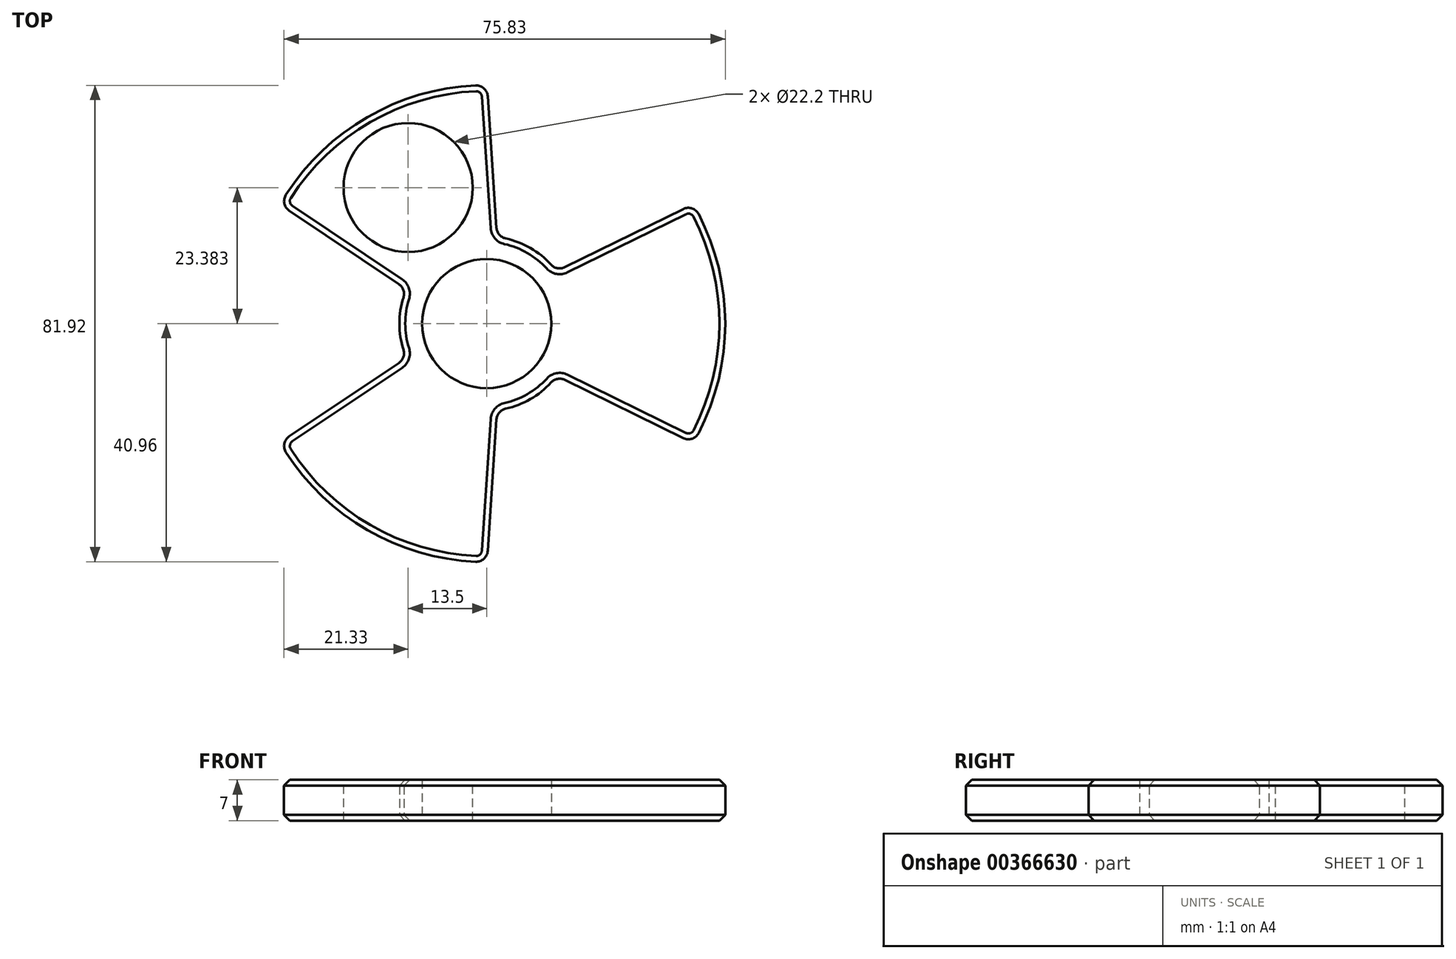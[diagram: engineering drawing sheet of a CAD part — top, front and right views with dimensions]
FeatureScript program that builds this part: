
annotation { "Feature Type Name" : "Feature", "Feature Type Description" : "" }
export const myFeature = defineFeature(function(context is Context, id is Id, definition is map)
    precondition{}
    {
        {
            var Q0;
            Q0=qCreatedBy(makeId("Top.planeOp"),FACE);
            var sketch = newSketch(context, id + "F0", { "sketchPlane" : qUnion([Q0])});
            skCircle(sketch, "E0", {"center": v(0, 0) * mm, "radius": 15 * mm});
            skCircle(sketch, "E1", {"center": v(0, 0) * mm, "radius": 41 * mm});
            skCircle(sketch, "E2", {"center": v(0, 0) * mm, "radius": 11.1 * mm});
            skLineSegment(sketch, "E3", {"start": v(0, 15) * mm, "end": v(0, 41) * mm});
            skLineSegment(sketch, "E4.1.0", {"start": v(-13, 7.5) * mm, "end": v(-35.5, 20.5) * mm});
            skLineSegment(sketch, "E4.2.0", {"start": v(-13, -7.5) * mm, "end": v(-35.5, -20.5) * mm});
            skLineSegment(sketch, "E4.3.0", {"start": v(0, -15) * mm, "end": v(0, -41) * mm});
            skLineSegment(sketch, "E4.4.0", {"start": v(13, -7.5) * mm, "end": v(35.5, -20.5) * mm});
            skLineSegment(sketch, "E4.5.0", {"start": v(13, 7.5) * mm, "end": v(35.5, 20.5) * mm});
            skSolve(sketch);
        }
        {
            var Q0;
            {var subQ0=sQuery(id+"F0.wireOp",EDGE,"E3");Q0=makeQuery(id+"F0.imprint","IMPRINT",FACE,{"disambiguationData":[TD([[makeQuery(id+"F0.imprint","IMPRINT",EDGE,{"derivedFrom":subQ0}),1.0]])]});}
            var Q1;
            {var subQ0=sQuery(id+"F0.wireOp",EDGE,"E4.4.0");Q1=makeQuery(id+"F0.imprint","IMPRINT",FACE,{"disambiguationData":[TD([[makeQuery(id+"F0.imprint","IMPRINT",EDGE,{"derivedFrom":subQ0}),1.0]])]});}
            var Q2;
            {var subQ0=sQuery(id+"F0.wireOp",EDGE,"E4.2.0");Q2=makeQuery(id+"F0.imprint","IMPRINT",FACE,{"disambiguationData":[TD([[makeQuery(id+"F0.imprint","IMPRINT",EDGE,{"derivedFrom":subQ0}),1.0]])]});}
            var Q3;
            Q3=makeQuery(id+"F0.imprint","IMPRINT",FACE,{"disambiguationData":[TD([[makeQuery(id+"F0.imprint","IMPRINT",EDGE,{"derivedFrom":sQuery(id+"F0.wireOp",EDGE,"E2")}),-1.0]])]});
            extrude(context, id + "F1", {"entities" : qUnion([Q0, Q1, Q2, Q3]), "depth" : 7 * mm});
        }
        {
            var Q0;
            Q0=makeQuery(id+"F1.opExtrude","SWEPT_EDGE",EDGE,{"disambiguationData":[OSD([sQuery(id+"F0.wireOp",EDGE,"E0"),sQuery(id+"F0.wireOp",EDGE,"E4.1.0")])]});
            var Q1;
            Q1=makeQuery(id+"F1.opExtrude","SWEPT_EDGE",EDGE,{"disambiguationData":[OSD([sQuery(id+"F0.wireOp",EDGE,"E0"),sQuery(id+"F0.wireOp",EDGE,"E4.2.0")])]});
            var Q2;
            Q2=makeQuery(id+"F1.opExtrude","SWEPT_EDGE",EDGE,{"disambiguationData":[OSD([sQuery(id+"F0.wireOp",EDGE,"E0"),sQuery(id+"F0.wireOp",EDGE,"E4.3.0")])]});
            var Q3;
            Q3=makeQuery(id+"F1.opExtrude","SWEPT_EDGE",EDGE,{"disambiguationData":[OSD([sQuery(id+"F0.wireOp",EDGE,"E0"),sQuery(id+"F0.wireOp",EDGE,"E4.5.0")])]});
            chamfer(context, id + "F2", {"entities" : qUnion([Q0, Q1, Q2, Q3]), "chamferType" : ChamferType.TWO_OFFSETS, "width1" : 5 * mm, "oppositeDirection" : false, "width2" : 27 * mm, "tangentPropagation" : true});
        }
        {
            var Q0;
            Q0=makeQuery(id+"F1.opExtrude","SWEPT_EDGE",EDGE,{"disambiguationData":[OSD([sQuery(id+"F0.wireOp",EDGE,"E0"),sQuery(id+"F0.wireOp",EDGE,"E4.4.0")])]});
            var Q1;
            Q1=makeQuery(id+"F1.opExtrude","SWEPT_EDGE",EDGE,{"disambiguationData":[OSD([sQuery(id+"F0.wireOp",EDGE,"E0"),sQuery(id+"F0.wireOp",EDGE,"E3")])]});
            chamfer(context, id + "F3", {"entities" : qUnion([Q0, Q1]), "chamferType" : ChamferType.TWO_OFFSETS, "width1" : 27 * mm, "oppositeDirection" : false, "width2" : 5 * mm, "tangentPropagation" : true});
        }
        {
            var Q0;
            {var subQ0=sQuery(id+"F0.wireOp",EDGE,"E1");var subQ1=sQuery(id+"F0.wireOp",EDGE,"E4.1.0");Q0=makeQuery(id+"F2.opChamfer","BLEND_EDGE",EDGE,{"blendedFrom":[makeQuery(id+"F1.opExtrude","SWEPT_EDGE",EDGE,{"disambiguationData":[OSD([sQuery(id+"F0.wireOp",EDGE,"E0"),subQ1])]}),makeQuery(id+"F1.opExtrude","SWEPT_FACE",FACE,{"disambiguationData":[OSD([subQ0]),TDD([makeQuery(id+"F0.imprint","IMPRINT",EDGE,{"disambiguationData":[TD([[makeQuery(id+"F0.imprint","INTERSECT",VERTEX,{"derivedFrom":[subQ0,sQuery(id+"F0.wireOp",EDGE,"E3")]}),-1.0]])],"derivedFrom":subQ0})])]})],"blendedInto":[makeQuery(id+"F1.opExtrude","SWEPT_FACE",FACE,{"disambiguationData":[OSD([subQ0]),TDD([makeQuery(id+"F0.imprint","IMPRINT",EDGE,{"disambiguationData":[TD([[makeQuery(id+"F0.imprint","INTERSECT",VERTEX,{"derivedFrom":[subQ0,sQuery(id+"F0.wireOp",EDGE,"E3")]}),-1.0]])],"derivedFrom":subQ0})])]})]});}
            var Q1;
            {var subQ0=sQuery(id+"F0.wireOp",EDGE,"E3");var subQ1=sQuery(id+"F0.wireOp",EDGE,"E1");Q1=makeQuery(id+"F3.opChamfer","BLEND_EDGE",EDGE,{"blendedFrom":[makeQuery(id+"F1.opExtrude","SWEPT_EDGE",EDGE,{"disambiguationData":[OSD([sQuery(id+"F0.wireOp",EDGE,"E0"),subQ0])]}),makeQuery(id+"F1.opExtrude","SWEPT_FACE",FACE,{"disambiguationData":[OSD([subQ1]),TDD([makeQuery(id+"F0.imprint","IMPRINT",EDGE,{"disambiguationData":[TD([[makeQuery(id+"F0.imprint","INTERSECT",VERTEX,{"derivedFrom":[subQ1,subQ0]}),-1.0]])],"derivedFrom":subQ1})])]})],"blendedInto":[makeQuery(id+"F1.opExtrude","SWEPT_FACE",FACE,{"disambiguationData":[OSD([subQ1]),TDD([makeQuery(id+"F0.imprint","IMPRINT",EDGE,{"disambiguationData":[TD([[makeQuery(id+"F0.imprint","INTERSECT",VERTEX,{"derivedFrom":[subQ1,subQ0]}),-1.0]])],"derivedFrom":subQ1})])]})]});}
            var Q2;
            {var subQ0=sQuery(id+"F0.wireOp",EDGE,"E3");var subQ1=sQuery(id+"F0.wireOp",EDGE,"E0");Q2=makeQuery(id+"F3.opChamfer","BLEND_EDGE",EDGE,{"blendedFrom":[makeQuery(id+"F1.opExtrude","SWEPT_EDGE",EDGE,{"disambiguationData":[OSD([subQ1,subQ0])]}),makeQuery(id+"F1.opExtrude","SWEPT_FACE",FACE,{"disambiguationData":[OSD([subQ1]),TDD([makeQuery(id+"F0.imprint","IMPRINT",EDGE,{"disambiguationData":[TD([[makeQuery(id+"F0.imprint","INTERSECT",VERTEX,{"derivedFrom":[subQ1,subQ0]}),1.0]])],"derivedFrom":subQ1})])]})],"blendedInto":[makeQuery(id+"F1.opExtrude","SWEPT_FACE",FACE,{"disambiguationData":[OSD([subQ1]),TDD([makeQuery(id+"F0.imprint","IMPRINT",EDGE,{"disambiguationData":[TD([[makeQuery(id+"F0.imprint","INTERSECT",VERTEX,{"derivedFrom":[subQ1,subQ0]}),1.0]])],"derivedFrom":subQ1})])]})]});}
            var Q3;
            {var subQ0=sQuery(id+"F0.wireOp",EDGE,"E0");var subQ1=sQuery(id+"F0.wireOp",EDGE,"E4.5.0");Q3=makeQuery(id+"F2.opChamfer","BLEND_EDGE",EDGE,{"blendedFrom":[makeQuery(id+"F1.opExtrude","SWEPT_EDGE",EDGE,{"disambiguationData":[OSD([subQ0,subQ1])]}),makeQuery(id+"F1.opExtrude","SWEPT_FACE",FACE,{"disambiguationData":[OSD([subQ0]),TDD([makeQuery(id+"F0.imprint","IMPRINT",EDGE,{"disambiguationData":[TD([[makeQuery(id+"F0.imprint","INTERSECT",VERTEX,{"derivedFrom":[subQ0,sQuery(id+"F0.wireOp",EDGE,"E3")]}),1.0]])],"derivedFrom":subQ0})])]})],"blendedInto":[makeQuery(id+"F1.opExtrude","SWEPT_FACE",FACE,{"disambiguationData":[OSD([subQ0]),TDD([makeQuery(id+"F0.imprint","IMPRINT",EDGE,{"disambiguationData":[TD([[makeQuery(id+"F0.imprint","INTERSECT",VERTEX,{"derivedFrom":[subQ0,sQuery(id+"F0.wireOp",EDGE,"E3")]}),1.0]])],"derivedFrom":subQ0})])]})]});}
            var Q4;
            {var subQ0=sQuery(id+"F0.wireOp",EDGE,"E1");var subQ1=sQuery(id+"F0.wireOp",EDGE,"E4.5.0");Q4=makeQuery(id+"F2.opChamfer","BLEND_EDGE",EDGE,{"blendedFrom":[makeQuery(id+"F1.opExtrude","SWEPT_EDGE",EDGE,{"disambiguationData":[OSD([sQuery(id+"F0.wireOp",EDGE,"E0"),subQ1])]}),makeQuery(id+"F1.opExtrude","SWEPT_FACE",FACE,{"disambiguationData":[OSD([subQ0]),TDD([makeQuery(id+"F0.imprint","IMPRINT",EDGE,{"disambiguationData":[TD([[makeQuery(id+"F0.imprint","INTERSECT",VERTEX,{"derivedFrom":[subQ0,sQuery(id+"F0.wireOp",EDGE,"E4.4.0")]}),-1.0]])],"derivedFrom":subQ0})])]})],"blendedInto":[makeQuery(id+"F1.opExtrude","SWEPT_FACE",FACE,{"disambiguationData":[OSD([subQ0]),TDD([makeQuery(id+"F0.imprint","IMPRINT",EDGE,{"disambiguationData":[TD([[makeQuery(id+"F0.imprint","INTERSECT",VERTEX,{"derivedFrom":[subQ0,sQuery(id+"F0.wireOp",EDGE,"E4.4.0")]}),-1.0]])],"derivedFrom":subQ0})])]})]});}
            var Q5;
            {var subQ0=sQuery(id+"F0.wireOp",EDGE,"E4.4.0");var subQ1=sQuery(id+"F0.wireOp",EDGE,"E1");Q5=makeQuery(id+"F3.opChamfer","BLEND_EDGE",EDGE,{"blendedFrom":[makeQuery(id+"F1.opExtrude","SWEPT_EDGE",EDGE,{"disambiguationData":[OSD([sQuery(id+"F0.wireOp",EDGE,"E0"),subQ0])]}),makeQuery(id+"F1.opExtrude","SWEPT_FACE",FACE,{"disambiguationData":[OSD([subQ1]),TDD([makeQuery(id+"F0.imprint","IMPRINT",EDGE,{"disambiguationData":[TD([[makeQuery(id+"F0.imprint","INTERSECT",VERTEX,{"derivedFrom":[subQ1,subQ0]}),-1.0]])],"derivedFrom":subQ1})])]})],"blendedInto":[makeQuery(id+"F1.opExtrude","SWEPT_FACE",FACE,{"disambiguationData":[OSD([subQ1]),TDD([makeQuery(id+"F0.imprint","IMPRINT",EDGE,{"disambiguationData":[TD([[makeQuery(id+"F0.imprint","INTERSECT",VERTEX,{"derivedFrom":[subQ1,subQ0]}),-1.0]])],"derivedFrom":subQ1})])]})]});}
            var Q6;
            {var subQ0=sQuery(id+"F0.wireOp",EDGE,"E0");var subQ1=sQuery(id+"F0.wireOp",EDGE,"E4.4.0");Q6=makeQuery(id+"F3.opChamfer","BLEND_EDGE",EDGE,{"blendedFrom":[makeQuery(id+"F1.opExtrude","SWEPT_EDGE",EDGE,{"disambiguationData":[OSD([subQ0,subQ1])]}),makeQuery(id+"F1.opExtrude","SWEPT_FACE",FACE,{"disambiguationData":[OSD([subQ0]),TDD([makeQuery(id+"F0.imprint","IMPRINT",EDGE,{"disambiguationData":[TD([[makeQuery(id+"F0.imprint","INTERSECT",VERTEX,{"derivedFrom":[subQ0,sQuery(id+"F0.wireOp",EDGE,"E4.3.0")]}),-1.0]])],"derivedFrom":subQ0})])]})],"blendedInto":[makeQuery(id+"F1.opExtrude","SWEPT_FACE",FACE,{"disambiguationData":[OSD([subQ0]),TDD([makeQuery(id+"F0.imprint","IMPRINT",EDGE,{"disambiguationData":[TD([[makeQuery(id+"F0.imprint","INTERSECT",VERTEX,{"derivedFrom":[subQ0,sQuery(id+"F0.wireOp",EDGE,"E4.3.0")]}),-1.0]])],"derivedFrom":subQ0})])]})]});}
            var Q7;
            {var subQ0=sQuery(id+"F0.wireOp",EDGE,"E4.3.0");var subQ1=sQuery(id+"F0.wireOp",EDGE,"E0");Q7=makeQuery(id+"F2.opChamfer","BLEND_EDGE",EDGE,{"blendedFrom":[makeQuery(id+"F1.opExtrude","SWEPT_EDGE",EDGE,{"disambiguationData":[OSD([subQ1,subQ0])]}),makeQuery(id+"F1.opExtrude","SWEPT_FACE",FACE,{"disambiguationData":[OSD([subQ1]),TDD([makeQuery(id+"F0.imprint","IMPRINT",EDGE,{"disambiguationData":[TD([[makeQuery(id+"F0.imprint","INTERSECT",VERTEX,{"derivedFrom":[subQ1,subQ0]}),-1.0]])],"derivedFrom":subQ1})])]})],"blendedInto":[makeQuery(id+"F1.opExtrude","SWEPT_FACE",FACE,{"disambiguationData":[OSD([subQ1]),TDD([makeQuery(id+"F0.imprint","IMPRINT",EDGE,{"disambiguationData":[TD([[makeQuery(id+"F0.imprint","INTERSECT",VERTEX,{"derivedFrom":[subQ1,subQ0]}),-1.0]])],"derivedFrom":subQ1})])]})]});}
            var Q8;
            {var subQ0=sQuery(id+"F0.wireOp",EDGE,"E1");var subQ1=sQuery(id+"F0.wireOp",EDGE,"E4.3.0");Q8=makeQuery(id+"F2.opChamfer","BLEND_EDGE",EDGE,{"blendedFrom":[makeQuery(id+"F1.opExtrude","SWEPT_EDGE",EDGE,{"disambiguationData":[OSD([sQuery(id+"F0.wireOp",EDGE,"E0"),subQ1])]}),makeQuery(id+"F1.opExtrude","SWEPT_FACE",FACE,{"disambiguationData":[OSD([subQ0]),TDD([makeQuery(id+"F0.imprint","IMPRINT",EDGE,{"disambiguationData":[TD([[makeQuery(id+"F0.imprint","INTERSECT",VERTEX,{"derivedFrom":[subQ0,sQuery(id+"F0.wireOp",EDGE,"E4.2.0")]}),-1.0]])],"derivedFrom":subQ0})])]})],"blendedInto":[makeQuery(id+"F1.opExtrude","SWEPT_FACE",FACE,{"disambiguationData":[OSD([subQ0]),TDD([makeQuery(id+"F0.imprint","IMPRINT",EDGE,{"disambiguationData":[TD([[makeQuery(id+"F0.imprint","INTERSECT",VERTEX,{"derivedFrom":[subQ0,sQuery(id+"F0.wireOp",EDGE,"E4.2.0")]}),-1.0]])],"derivedFrom":subQ0})])]})]});}
            var Q9;
            {var subQ0=sQuery(id+"F0.wireOp",EDGE,"E4.2.0");var subQ1=sQuery(id+"F0.wireOp",EDGE,"E1");Q9=makeQuery(id+"F2.opChamfer","BLEND_EDGE",EDGE,{"blendedFrom":[makeQuery(id+"F1.opExtrude","SWEPT_EDGE",EDGE,{"disambiguationData":[OSD([sQuery(id+"F0.wireOp",EDGE,"E0"),subQ0])]}),makeQuery(id+"F1.opExtrude","SWEPT_FACE",FACE,{"disambiguationData":[OSD([subQ1]),TDD([makeQuery(id+"F0.imprint","IMPRINT",EDGE,{"disambiguationData":[TD([[makeQuery(id+"F0.imprint","INTERSECT",VERTEX,{"derivedFrom":[subQ1,subQ0]}),-1.0]])],"derivedFrom":subQ1})])]})],"blendedInto":[makeQuery(id+"F1.opExtrude","SWEPT_FACE",FACE,{"disambiguationData":[OSD([subQ1]),TDD([makeQuery(id+"F0.imprint","IMPRINT",EDGE,{"disambiguationData":[TD([[makeQuery(id+"F0.imprint","INTERSECT",VERTEX,{"derivedFrom":[subQ1,subQ0]}),-1.0]])],"derivedFrom":subQ1})])]})]});}
            var Q10;
            {var subQ0=sQuery(id+"F0.wireOp",EDGE,"E0");var subQ1=sQuery(id+"F0.wireOp",EDGE,"E4.2.0");Q10=makeQuery(id+"F2.opChamfer","BLEND_EDGE",EDGE,{"blendedFrom":[makeQuery(id+"F1.opExtrude","SWEPT_EDGE",EDGE,{"disambiguationData":[OSD([subQ0,subQ1])]}),makeQuery(id+"F1.opExtrude","SWEPT_FACE",FACE,{"disambiguationData":[OSD([subQ0]),TDD([makeQuery(id+"F0.imprint","IMPRINT",EDGE,{"disambiguationData":[TD([[makeQuery(id+"F0.imprint","INTERSECT",VERTEX,{"derivedFrom":[subQ0,sQuery(id+"F0.wireOp",EDGE,"E4.1.0")]}),-1.0]])],"derivedFrom":subQ0})])]})],"blendedInto":[makeQuery(id+"F1.opExtrude","SWEPT_FACE",FACE,{"disambiguationData":[OSD([subQ0]),TDD([makeQuery(id+"F0.imprint","IMPRINT",EDGE,{"disambiguationData":[TD([[makeQuery(id+"F0.imprint","INTERSECT",VERTEX,{"derivedFrom":[subQ0,sQuery(id+"F0.wireOp",EDGE,"E4.1.0")]}),-1.0]])],"derivedFrom":subQ0})])]})]});}
            var Q11;
            {var subQ0=sQuery(id+"F0.wireOp",EDGE,"E4.1.0");var subQ1=sQuery(id+"F0.wireOp",EDGE,"E0");Q11=makeQuery(id+"F2.opChamfer","BLEND_EDGE",EDGE,{"blendedFrom":[makeQuery(id+"F1.opExtrude","SWEPT_EDGE",EDGE,{"disambiguationData":[OSD([subQ1,subQ0])]}),makeQuery(id+"F1.opExtrude","SWEPT_FACE",FACE,{"disambiguationData":[OSD([subQ1]),TDD([makeQuery(id+"F0.imprint","IMPRINT",EDGE,{"disambiguationData":[TD([[makeQuery(id+"F0.imprint","INTERSECT",VERTEX,{"derivedFrom":[subQ1,subQ0]}),-1.0]])],"derivedFrom":subQ1})])]})],"blendedInto":[makeQuery(id+"F1.opExtrude","SWEPT_FACE",FACE,{"disambiguationData":[OSD([subQ1]),TDD([makeQuery(id+"F0.imprint","IMPRINT",EDGE,{"disambiguationData":[TD([[makeQuery(id+"F0.imprint","INTERSECT",VERTEX,{"derivedFrom":[subQ1,subQ0]}),-1.0]])],"derivedFrom":subQ1})])]})]});}
            fillet(context, id + "F4", {"entities" : qUnion([Q0, Q1, Q2, Q3, Q4, Q5, Q6, Q7, Q8, Q9, Q10, Q11]), "radius" : 2 * mm, "tangentPropagation" : true, "allowEdgeOverflow" : false});
        }
        {
            var Q0;
            {var subQ0=sQuery(id+"F0.wireOp",EDGE,"E1");Q0=makeQuery(id+"F1.opExtrude","CAP_EDGE",EDGE,{"disambiguationData":[OSD([subQ0]),TDD([makeQuery(id+"F0.imprint","IMPRINT",EDGE,{"disambiguationData":[TD([[makeQuery(id+"F0.imprint","INTERSECT",VERTEX,{"derivedFrom":[subQ0,sQuery(id+"F0.wireOp",EDGE,"E4.4.0")]}),-1.0]])],"derivedFrom":subQ0})])],"isStart":false});}
            var Q1;
            {var subQ0=sQuery(id+"F0.wireOp",EDGE,"E1");Q1=makeQuery(id+"F1.opExtrude","CAP_EDGE",EDGE,{"disambiguationData":[OSD([subQ0]),TDD([makeQuery(id+"F0.imprint","IMPRINT",EDGE,{"disambiguationData":[TD([[makeQuery(id+"F0.imprint","INTERSECT",VERTEX,{"derivedFrom":[subQ0,sQuery(id+"F0.wireOp",EDGE,"E4.4.0")]}),-1.0]])],"derivedFrom":subQ0})])],"isStart":true});}
            chamfer(context, id + "F5", {"entities" : qUnion([Q0, Q1]), "width" : 1 * mm, "tangentPropagation" : true});
        }
        {
            var Q0;
            Q0=makeQuery(id+"F1.opExtrude","CAP_FACE",FACE,{"disambiguationData":[OSD([sQuery(id+"F0.wireOp",EDGE,"E0"),sQuery(id+"F0.wireOp",EDGE,"E1"),sQuery(id+"F0.wireOp",EDGE,"E2"),sQuery(id+"F0.wireOp",EDGE,"E3"),sQuery(id+"F0.wireOp",EDGE,"E4.1.0"),sQuery(id+"F0.wireOp",EDGE,"E4.2.0"),sQuery(id+"F0.wireOp",EDGE,"E4.3.0"),sQuery(id+"F0.wireOp",EDGE,"E4.4.0"),sQuery(id+"F0.wireOp",EDGE,"E4.5.0")])],"isStart":false});
            var sketch = newSketch(context, id + "F6", { "sketchPlane" : qUnion([Q0])});
            skCircle(sketch, "E5", {"center": v(-13.5, 23.38) * mm, "radius": 11.1 * mm});
            skLineSegment(sketch, "E6", {"start": v(0, 0) * mm, "end": v(-13.5, 23.38) * mm, "construction": true});
            skLineSegment(sketch, "E7", {"start": v(0, 0) * mm, "end": v(0, 11.1) * mm, "construction": true});
            skSolve(sketch);
        }
        {
            var Q0;
            Q0=makeQuery(id+"F6.imprint","IMPRINT",FACE,{"disambiguationData":[TD([[makeQuery(id+"F6.imprint","IMPRINT",EDGE,{"derivedFrom":sQuery(id+"F6.wireOp",EDGE,"E5")}),1.0]])]});
            extrude(context, id + "F7", {"entities" : qUnion([Q0]), "operationType" : NewBodyOperationType.REMOVE, "endBound" : BoundingType.THROUGH_ALL, "oppositeDirection" : true, "depth" : 25 * mm});
        }
    });
